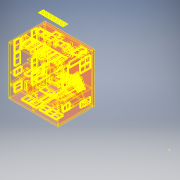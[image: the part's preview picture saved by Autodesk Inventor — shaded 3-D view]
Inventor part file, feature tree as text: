
AUTODESK INVENTOR PART (.ipt)
format: ipt  version: 2017 (Build 210142000, 142)  size: 6,654,464 bytes
history: native  units: in
note: dims shown in document units (in); Inventor stores cm internally (conversion verified against a paired STEP export)
features: other x3, sketch x1
ambient origin geometry x8: Origin, YZ Plane, XZ Plane, XY Plane, X Axis, Y Axis, Z Axis, Center Point
bodies: Body1 (feature_tree), Body2 (feature_tree), Body3 (feature_tree), Body4 (feature_tree), Body5 (feature_tree), Body6 (feature_tree), Body7 (feature_tree), Body8 (feature_tree), Body9 (feature_tree), Body10 (feature_tree), Body11 (feature_tree), Body12 (feature_tree), Body13 (feature_tree), Body14 (feature_tree), Body15 (feature_tree), Body16 (feature_tree), Body17 (feature_tree), Body18 (feature_tree), Body19 (feature_tree), Body20 (feature_tree), Body21 (feature_tree), Body22 (feature_tree), Body23 (feature_tree), Body24 (feature_tree), Body25 (feature_tree), Body26 (feature_tree), Body27 (feature_tree), Body28 (feature_tree), Body29 (feature_tree), Body30 (feature_tree), Body31 (feature_tree), Body32 (feature_tree), Body33 (feature_tree), Body34 (feature_tree), Body35 (feature_tree), Body36 (feature_tree), Body37 (feature_tree), Body38 (feature_tree), Body39 (feature_tree), Body40 (feature_tree), Body41 (feature_tree), Body42 (feature_tree), Body43 (feature_tree), Body44 (feature_tree), Body45 (feature_tree), Body46 (feature_tree), Body47 (feature_tree), Body48 (feature_tree), Body49 (feature_tree), Body50 (feature_tree), Body51 (feature_tree), Body52 (feature_tree), Body53 (feature_tree), Body54 (feature_tree), Body55 (feature_tree), Body56 (feature_tree), Body57 (feature_tree), Body58 (feature_tree), Body59 (feature_tree), Body60 (feature_tree), Body61 (feature_tree), Body62 (feature_tree), Body63 (feature_tree), Body64 (feature_tree), Body65 (feature_tree), Body66 (feature_tree), Body67 (feature_tree), Body68 (feature_tree), Body69 (feature_tree), Body70 (feature_tree), Body71 (feature_tree), Body72 (feature_tree), Body73 (feature_tree), Body74 (feature_tree), Body75 (feature_tree), Body76 (feature_tree), Body77 (feature_tree), Body78 (feature_tree), Body79 (feature_tree), Body80 (feature_tree), Body81 (feature_tree), Body82 (feature_tree), Body83 (feature_tree), Body84 (feature_tree), Body85 (feature_tree), Body86 (feature_tree), Body87 (feature_tree), Body88 (feature_tree), Body89 (feature_tree), Body90 (feature_tree), Body91 (feature_tree), Body92 (feature_tree), Body93 (feature_tree), Body94 (feature_tree), Body95 (feature_tree), Body96 (feature_tree), Body97 (feature_tree), Body98 (feature_tree), Body99 (feature_tree), Body100 (feature_tree), Body101 (feature_tree), Body102 (feature_tree), Body103 (feature_tree), Body104 (feature_tree), Body105 (feature_tree), Body106 (feature_tree), Body107 (feature_tree), Body108 (feature_tree), Body109 (feature_tree), Body110 (feature_tree), Body111 (feature_tree), Body112 (feature_tree), Body113 (feature_tree), Body114 (feature_tree), Body115 (feature_tree), Body116 (feature_tree), Body117 (feature_tree), Body118 (feature_tree), Body119 (feature_tree), Body120 (feature_tree), Body121 (feature_tree), Body122 (feature_tree), Body123 (feature_tree), Body124 (feature_tree), Body125 (feature_tree), Body126 (feature_tree), Body127 (feature_tree), Body128 (feature_tree), Body129 (feature_tree), Body130 (feature_tree), Body131 (feature_tree), Body132 (feature_tree), Body133 (feature_tree), Body134 (feature_tree), Body135 (feature_tree), Body136 (feature_tree), Body137 (feature_tree), Body138 (feature_tree), Body139 (feature_tree), Body140 (feature_tree), Body141 (feature_tree), Body142 (feature_tree), Body143 (feature_tree), Body144 (feature_tree), Body145 (feature_tree), Body146 (feature_tree), Body147 (feature_tree), Body148 (feature_tree), Body149 (feature_tree), Body150 (feature_tree), Body151 (feature_tree), Body152 (feature_tree), Body153 (feature_tree), Body154 (feature_tree), Body155 (feature_tree), Body156 (feature_tree), Body157 (feature_tree), Body158 (feature_tree), Body159 (feature_tree), Body160 (feature_tree), Body161 (feature_tree), Body162 (feature_tree), Body163 (feature_tree), Body164 (feature_tree), Body165 (feature_tree), Body166 (feature_tree), Body167 (feature_tree), Body168 (feature_tree), Body169 (feature_tree), Body170 (feature_tree), Body171 (feature_tree), Body172 (feature_tree), Body173 (feature_tree), Body174 (feature_tree), Body175 (feature_tree), Body176 (feature_tree), Body177 (feature_tree), Body178 (feature_tree), Body179 (feature_tree), Body180 (feature_tree), Body181 (feature_tree), Body182 (feature_tree), Body183 (feature_tree), Body184 (feature_tree), Body185 (feature_tree), Body186 (feature_tree), Body187 (feature_tree), Body188 (feature_tree), Body189 (feature_tree), Body190 (feature_tree), Body191 (feature_tree), Body192 (feature_tree), Body193 (feature_tree), Body194 (feature_tree), Body195 (feature_tree), Body196 (feature_tree), Body197 (feature_tree), Body198 (feature_tree), Body199 (feature_tree), Body200 (feature_tree), Body201 (feature_tree), Body202 (feature_tree), Body203 (feature_tree), Body204 (feature_tree), Body205 (feature_tree), Body206 (feature_tree), Body207 (feature_tree), Body208 (feature_tree), Body209 (feature_tree), Body210 (feature_tree), Body211 (feature_tree), Body212 (feature_tree), Body213 (feature_tree), Body214 (feature_tree), Body215 (feature_tree), Body216 (feature_tree), Body217 (feature_tree), Body218 (feature_tree), Body219 (feature_tree), Body220 (feature_tree), Body221 (feature_tree), Body222 (feature_tree), Body223 (feature_tree), Body224 (feature_tree), Body225 (feature_tree), Body226 (feature_tree), Body227 (feature_tree), Body228 (feature_tree), Body229 (feature_tree), Body230 (feature_tree), Body231 (feature_tree), Body232 (feature_tree), Body233 (feature_tree), Body234 (feature_tree), Body235 (feature_tree), Body236 (feature_tree), Body237 (feature_tree), Body238 (feature_tree), Body239 (feature_tree), Body240 (feature_tree), Body241 (feature_tree), Body242 (feature_tree), Body243 (feature_tree), Body244 (feature_tree), Body245 (feature_tree), Body246 (feature_tree), Body247 (feature_tree), Body248 (feature_tree), Body249 (feature_tree), Body250 (feature_tree), Body251 (feature_tree), Body252 (feature_tree), Body253 (feature_tree), Body254 (feature_tree), Body255 (feature_tree), Body256 (feature_tree), Body257 (feature_tree), Body258 (feature_tree), Body259 (feature_tree), Body260 (feature_tree), Body261 (feature_tree), Body262 (feature_tree), Body263 (feature_tree), Body264 (feature_tree), Body265 (feature_tree), Body266 (feature_tree), Body267 (feature_tree), Body268 (feature_tree), Body269 (feature_tree), Body270 (feature_tree), Body271 (feature_tree), Body272 (feature_tree), Body273 (feature_tree), Body274 (feature_tree), Body275 (feature_tree), Body276 (feature_tree), Body277 (feature_tree), Body278 (feature_tree), Body279 (feature_tree), Body280 (feature_tree), Body281 (feature_tree), Body282 (feature_tree), Body283 (feature_tree), Body284 (feature_tree), Body285 (feature_tree), Body286 (feature_tree), Body287 (feature_tree), Body288 (feature_tree), Body289 (feature_tree), Body290 (feature_tree), Body291 (feature_tree), Body292 (feature_tree), Body293 (feature_tree), Body294 (feature_tree), Body295 (feature_tree), Body296 (feature_tree), Body297 (feature_tree), Body298 (feature_tree), Body299 (feature_tree), Body300 (feature_tree), Body301 (feature_tree), Body302 (feature_tree), Body303 (feature_tree), Body304 (feature_tree), Body305 (feature_tree), Body306 (feature_tree), Body307 (feature_tree), Body308 (feature_tree), Body309 (feature_tree), Body310 (feature_tree), Body311 (feature_tree), Body312 (feature_tree), Body313 (feature_tree), Body314 (feature_tree), Body315 (feature_tree), Body316 (feature_tree), Body317 (feature_tree), Body318 (feature_tree), Body319 (feature_tree), Body320 (feature_tree), Body321 (feature_tree), Body322 (feature_tree), Body323 (feature_tree), Body324 (feature_tree), Body325 (feature_tree), Body326 (feature_tree), Body327 (feature_tree), Body328 (feature_tree), Body329 (feature_tree), Body330 (feature_tree), Body331 (feature_tree), Body332 (feature_tree), Body333 (feature_tree), Body334 (feature_tree), Body335 (feature_tree), Body336 (feature_tree), Body337 (feature_tree), Body338 (feature_tree), Body339 (feature_tree), Body340 (feature_tree), Body341 (feature_tree), Body342 (feature_tree), Body343 (feature_tree), Body344 (feature_tree), Body345 (feature_tree), Body346 (feature_tree), Body347 (feature_tree), Body348 (feature_tree), Body349 (feature_tree), Body350 (feature_tree), Body351 (feature_tree), Body352 (feature_tree), Body353 (feature_tree), Body354 (feature_tree), Body355 (feature_tree), Body356 (feature_tree), Body357 (feature_tree), Body358 (feature_tree), Body359 (feature_tree), Body360 (feature_tree), Body361 (feature_tree), Body362 (feature_tree), Body363 (feature_tree), Body364 (feature_tree), Body365 (feature_tree), Body366 (feature_tree), Body367 (feature_tree), Body368 (feature_tree), Body369 (feature_tree), Body370 (feature_tree), Body371 (feature_tree), Body372 (feature_tree), Body373 (feature_tree), Body374 (feature_tree), Body375 (feature_tree), Body376 (feature_tree), Body377 (feature_tree), Body378 (feature_tree), Body379 (feature_tree), Body380 (feature_tree), Body381 (feature_tree), Body382 (feature_tree), Body383 (feature_tree), Body384 (feature_tree), Body385 (feature_tree), Body386 (feature_tree), Body387 (feature_tree), Body388 (feature_tree), Body389 (feature_tree), Body390 (feature_tree), Body391 (feature_tree), Body392 (feature_tree), Body393 (feature_tree), Body394 (feature_tree), Body395 (feature_tree), Body396 (feature_tree), Body397 (feature_tree), Body398 (feature_tree), Body399 (feature_tree), Body400 (feature_tree), Body401 (feature_tree), Body402 (feature_tree), Body403 (feature_tree), Body404 (feature_tree), Body405 (feature_tree), Body406 (feature_tree), Body407 (feature_tree), Body408 (feature_tree), Body409 (feature_tree), Body410 (feature_tree), Body411 (feature_tree), Body412 (feature_tree), Body413 (feature_tree), Body414 (feature_tree), Body415 (feature_tree), Body416 (feature_tree), Body417 (feature_tree), Body418 (feature_tree), Body419 (feature_tree), Body420 (feature_tree), Body421 (feature_tree), Body422 (feature_tree), Body423 (feature_tree), Body424 (feature_tree), Body425 (feature_tree), Body426 (feature_tree), Body427 (feature_tree), Body428 (feature_tree), Body429 (feature_tree), Body430 (feature_tree), Body431 (feature_tree), Body432 (feature_tree), Body433 (feature_tree), Body434 (feature_tree), Body435 (feature_tree), Body436 (feature_tree), Body437 (feature_tree), Body438 (feature_tree), Body439 (feature_tree), Body440 (feature_tree), Body441 (feature_tree), Body442 (feature_tree), Body443 (feature_tree), Body444 (feature_tree), Body445 (feature_tree), Body446 (feature_tree), Body447 (feature_tree), Body448 (feature_tree), Body449 (feature_tree), Body450 (feature_tree), Body451 (feature_tree), Body452 (feature_tree), Body453 (feature_tree), Body454 (feature_tree), Body455 (feature_tree), Body456 (feature_tree), Body457 (feature_tree), Body458 (feature_tree), Body459 (feature_tree), Body460 (feature_tree), Body461 (feature_tree), Body462 (feature_tree), Body463 (feature_tree), Body464 (feature_tree), Body465 (feature_tree), Body466 (feature_tree), Body467 (feature_tree), Body468 (feature_tree), Body469 (feature_tree), Body470 (feature_tree), Body471 (feature_tree), Body472 (feature_tree), Body473 (feature_tree), Body474 (feature_tree), Body475 (feature_tree), Body476 (feature_tree), Body477 (feature_tree), Body478 (feature_tree), Body479 (feature_tree), Body480 (feature_tree), Body481 (feature_tree), Body482 (feature_tree), Body483 (feature_tree), Body484 (feature_tree), Body485 (feature_tree), Body486 (feature_tree), Body487 (feature_tree), Body488 (feature_tree), Body489 (feature_tree), Body490 (feature_tree), Body491 (feature_tree), Body492 (feature_tree), Body493 (feature_tree), Body494 (feature_tree), Body495 (feature_tree), Body496 (feature_tree), Body497 (feature_tree), Body498 (feature_tree), Body499 (feature_tree), Body500 (feature_tree), Body501 (feature_tree), Body502 (feature_tree), Body503 (feature_tree), Body504 (feature_tree), Body505 (feature_tree), Body506 (feature_tree), Body507 (feature_tree), Body508 (feature_tree), Body509 (feature_tree), Body510 (feature_tree), Body511 (feature_tree), Body512 (feature_tree), Body513 (feature_tree), Body514 (feature_tree), Body515 (feature_tree), Body516 (feature_tree), Body517 (feature_tree), Body518 (feature_tree), Body519 (feature_tree), Body520 (feature_tree), Body521 (feature_tree), Body522 (feature_tree), Body523 (feature_tree), Body524 (feature_tree), Body525 (feature_tree), Body526 (feature_tree), Body527 (feature_tree), Body528 (feature_tree), Body529 (feature_tree), Body530 (feature_tree), Body531 (feature_tree), Body532 (feature_tree), Body533 (feature_tree), Body534 (feature_tree), Body535 (feature_tree), Body536 (feature_tree), Body537 (feature_tree), Body538 (feature_tree), Body539 (feature_tree), Body540 (feature_tree), Body541 (feature_tree), Body542 (feature_tree), Body543 (feature_tree), Body544 (feature_tree), Body545 (feature_tree), Body546 (feature_tree), Body547 (feature_tree), Body548 (feature_tree), Body549 (feature_tree), Body550 (feature_tree), Body551 (feature_tree), Body552 (feature_tree), Body553 (feature_tree), Body554 (feature_tree), Body555 (feature_tree), Body556 (feature_tree), Body557 (feature_tree), Body558 (feature_tree), Body559 (feature_tree), Body560 (feature_tree), Body561 (feature_tree), Body562 (feature_tree), Body563 (feature_tree), Body564 (feature_tree), Body565 (feature_tree), Body566 (feature_tree), Body567 (feature_tree), Body568 (feature_tree), Body569 (feature_tree), Body570 (feature_tree), Body571 (feature_tree), Body572 (feature_tree), Body573 (feature_tree), Body574 (feature_tree), Body575 (feature_tree), Body576 (feature_tree), Body577 (feature_tree), Body578 (feature_tree), Body579 (feature_tree), Body580 (feature_tree), Body581 (feature_tree), Body582 (feature_tree), Body583 (feature_tree), Body584 (feature_tree), Body585 (feature_tree), Body586 (feature_tree), Body587 (feature_tree), Body588 (feature_tree), Body589 (feature_tree), Body590 (feature_tree), Body591 (feature_tree), Body592 (feature_tree), Body593 (feature_tree), Body594 (feature_tree), Body595 (feature_tree), Body596 (feature_tree), Body597 (feature_tree), Body598 (feature_tree), Body599 (feature_tree), Body600 (feature_tree), Body601 (feature_tree), Body602 (feature_tree), Body603 (feature_tree), Body604 (feature_tree), Body605 (feature_tree), Body606 (feature_tree), Body607 (feature_tree), Body608 (feature_tree), Body609 (feature_tree), Body610 (feature_tree), Body611 (feature_tree), Body612 (feature_tree), Body613 (feature_tree), Body614 (feature_tree), Body615 (feature_tree), Body616 (feature_tree), Body617 (feature_tree), Body618 (feature_tree), Body619 (feature_tree), Body620 (feature_tree), Body621 (feature_tree), Body622 (feature_tree), Body623 (feature_tree), Body624 (feature_tree), Body625 (feature_tree), Body626 (feature_tree), Body627 (feature_tree), Body628 (feature_tree), Body629 (feature_tree), Body630 (feature_tree), Body631 (feature_tree), Body632 (feature_tree), Body633 (feature_tree), Body634 (feature_tree), Body635 (feature_tree), Body636 (feature_tree), Body637 (feature_tree), Body638 (feature_tree), Body639 (feature_tree), Body640 (feature_tree), Body641 (feature_tree), Body642 (feature_tree), Body643 (feature_tree), Body644 (feature_tree), Body645 (feature_tree), Body646 (feature_tree), Body647 (feature_tree), Body648 (feature_tree), Body649 (feature_tree), Body650 (feature_tree), Body651 (feature_tree), Body652 (feature_tree), Body653 (feature_tree), Body654 (feature_tree), Body655 (feature_tree), Body656 (feature_tree), Body657 (feature_tree), Body658 (feature_tree), Body659 (feature_tree), Body660 (feature_tree), Body661 (feature_tree), Body662 (feature_tree), Body663 (feature_tree), Body664 (feature_tree), Body665 (feature_tree), Body666 (feature_tree), Body667 (feature_tree), Body668 (feature_tree), Body669 (feature_tree), Body670 (feature_tree), Body671 (feature_tree), Body672 (feature_tree), Body673 (feature_tree), Body674 (feature_tree), Body675 (feature_tree), Body676 (feature_tree), Body677 (feature_tree), Body678 (feature_tree), Body679 (feature_tree), Body680 (feature_tree), Body681 (feature_tree), Body682 (feature_tree), Body683 (feature_tree), Body684 (feature_tree), Body685 (feature_tree), Body686 (feature_tree), Body687 (feature_tree), Body688 (feature_tree), Body689 (feature_tree), Body690 (feature_tree), Body691 (feature_tree), Body692 (feature_tree), Body693 (feature_tree), Body694 (feature_tree), Body695 (feature_tree), Body696 (feature_tree), Body697 (feature_tree), Body698 (feature_tree), Body699 (feature_tree), Body700 (feature_tree), Body701 (feature_tree), Body702 (feature_tree), Body703 (feature_tree), Body704 (feature_tree), Body705 (feature_tree), Body706 (feature_tree), Body707 (feature_tree), Body708 (feature_tree), Body709 (feature_tree), Body710 (feature_tree), Body711 (feature_tree), Body712 (feature_tree), Body713 (feature_tree), Body714 (feature_tree), Body715 (feature_tree), Body716 (feature_tree), Body717 (feature_tree), Body718 (feature_tree), Body719 (feature_tree), Body720 (feature_tree), Body721 (feature_tree), Body722 (feature_tree), Body723 (feature_tree), Body724 (feature_tree), Body725 (feature_tree), Body726 (feature_tree), Body727 (feature_tree), Body728 (feature_tree), Body729 (feature_tree), Body730 (feature_tree), Body731 (feature_tree), Body732 (feature_tree), Body733 (feature_tree), Body734 (feature_tree), Body735 (feature_tree), Body736 (feature_tree), Body737 (feature_tree), Body738 (feature_tree), Body739 (feature_tree), Body740 (feature_tree), Body741 (feature_tree), Body742 (feature_tree), Body743 (feature_tree), Body744 (feature_tree), Body745 (feature_tree), Body746 (feature_tree), Body747 (feature_tree), Body748 (feature_tree), Body749 (feature_tree), Body750 (feature_tree), Body751 (feature_tree), Body752 (feature_tree), Body753 (feature_tree), Body754 (feature_tree), Body755 (feature_tree), Body756 (feature_tree), Body757 (feature_tree), Body758 (feature_tree), Body759 (feature_tree), Body760 (feature_tree), Body761 (feature_tree)
feature tree (4):
  other  "Repaired Geometry1"
  sketch  "Sketch5"
  other  "Composite1"
  other  "Srf1"
